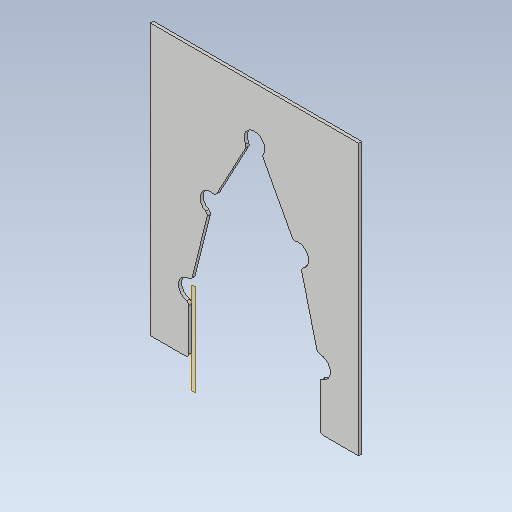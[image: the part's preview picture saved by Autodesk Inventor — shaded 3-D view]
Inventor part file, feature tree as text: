
AUTODESK INVENTOR PART (.ipt)
format: ipt  version: 2020.1 (Build 241239000, 239)  size: 207,872 bytes
history: native  units: mm
features: reference x11, other x4, plane x1, sheet_metal_op x1, sketch x1
ambient origin geometry x8: Origin, YZ Plane, XZ Plane, XY Plane, X Axis, Y Axis, Z Axis, Center Point
bodies: Solid1 (feature_tree)
feature tree (18):
  plane  "Work Plane1"
  sheet_metal_op  "Face1"
  sketch  "Sketch1"  dims[d0=200.0mm d1=100.0mm d2=260.0mm d3=50.0mm d4=10.0mm d5=10.0mm d6=10.0mm d7=10.0mm d8=10.0mm d9=3.0mm d10=3.0mm]
  reference  "Reference12"
  reference  "Reference13"
  reference  "Reference14"
  reference  "Reference15"
  reference  "Reference16"
  reference  "Reference17"
  reference  "Reference18"
  reference  "Reference19"
  reference  "Reference20"
  reference  "Reference21"
  reference  "Reference22"
  other  "Plate1"
  other  "Assembly1"
  other  "plade:1"
  other  "Definition1"
